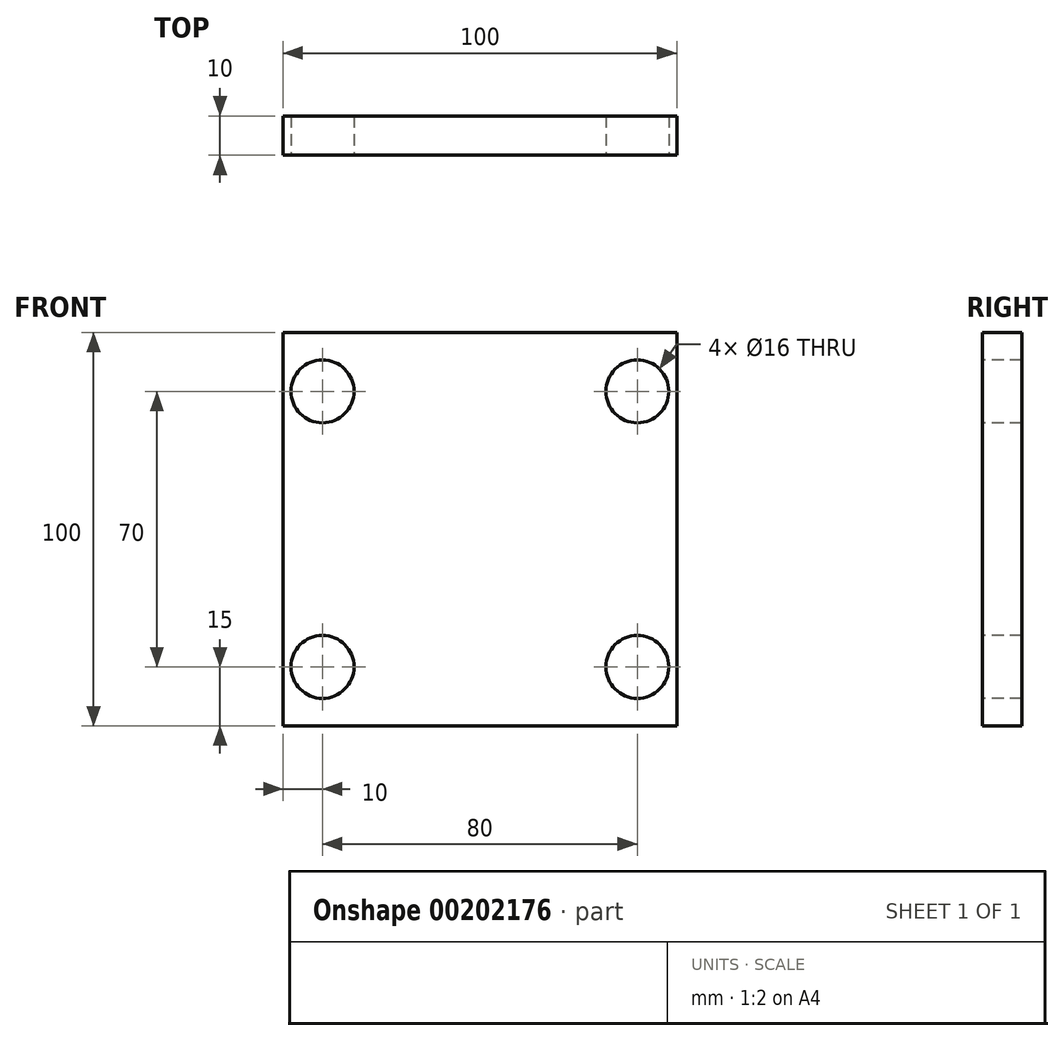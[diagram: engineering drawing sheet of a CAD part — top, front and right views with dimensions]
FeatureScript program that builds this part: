
annotation { "Feature Type Name" : "Feature", "Feature Type Description" : "" }
export const myFeature = defineFeature(function(context is Context, id is Id, definition is map)
    precondition{}
    {
        {
            var Q0;
            Q0=qCreatedBy(makeId("Front.planeOp"),FACE);
            var sketch = newSketch(context, id + "F0", { "sketchPlane" : qUnion([Q0])});
            skLineSegment(sketch, "E0.bottom", {"start": v(50, -50) * mm, "end": v(-50, -50) * mm});
            skLineSegment(sketch, "E0.top", {"start": v(50, 50) * mm, "end": v(-50, 50) * mm});
            skLineSegment(sketch, "E0.left", {"start": v(50, -50) * mm, "end": v(50, 50) * mm});
            skLineSegment(sketch, "E0.right", {"start": v(-50, -50) * mm, "end": v(-50, 50) * mm});
            skPoint(sketch, "E0.middle", {"position": v(0, 0) * mm});
            skSolve(sketch);
        }
        {
            var Q0;
            Q0=makeQuery(id+"F0.imprint","IMPRINT",FACE,{"disambiguationData":[TD([[makeQuery(id+"F0.imprint","IMPRINT",EDGE,{"derivedFrom":sQuery(id+"F0.wireOp",EDGE,"E0.bottom")}),-1.0]])]});
            extrude(context, id + "F1", {"entities" : qUnion([Q0]), "depth" : 10 * mm});
        }
        {
            var Q0;
            Q0=makeQuery(id+"F1.opExtrude","CAP_FACE",FACE,{"disambiguationData":[OSD([sQuery(id+"F0.wireOp",EDGE,"E0.bottom"),sQuery(id+"F0.wireOp",EDGE,"E0.top"),sQuery(id+"F0.wireOp",EDGE,"E0.left"),sQuery(id+"F0.wireOp",EDGE,"E0.right")])],"isStart":false});
            var sketch = newSketch(context, id + "F2", { "sketchPlane" : qUnion([Q0])});
            skLineSegment(sketch, "E1", {"start": v(0, 35) * mm, "end": v(40, 35) * mm, "construction": true});
            skLineSegment(sketch, "E2", {"start": v(0, 35) * mm, "end": v(-40, 35) * mm, "construction": true});
            skLineSegment(sketch, "E3", {"start": v(-40, 35) * mm, "end": v(-40, 0) * mm, "construction": true});
            skPoint(sketch, "E4.start.orphan", {"position": v(0, 50) * mm});
            skLineSegment(sketch, "E5", {"start": v(-40, 0) * mm, "end": v(-40, -35) * mm, "construction": true});
            skLineSegment(sketch, "E6", {"start": v(40, -35) * mm, "end": v(40, 35) * mm, "construction": true});
            skLineSegment(sketch, "E7", {"start": v(-40, -35) * mm, "end": v(40, -35) * mm, "construction": true});
            skSolve(sketch);
        }
        {
            var Q0;
            Q0=sQuery(id+"F2.wireOp",VERTEX,"E3.start");
            var Q1;
            Q1=sQuery(id+"F2.wireOp",VERTEX,"E1.end");
            var Q2;
            Q2=sQuery(id+"F2.wireOp",VERTEX,"E7.start");
            var Q3;
            Q3=sQuery(id+"F2.wireOp",VERTEX,"E7.end");
            var Q4;
            Q4=makeQuery(id+"F1.opExtrude","SWEPT_BODY",BODY,{"disambiguationData":[OSD([sQuery(id+"F0.wireOp",EDGE,"E0.bottom"),sQuery(id+"F0.wireOp",EDGE,"E0.top"),sQuery(id+"F0.wireOp",EDGE,"E0.left"),sQuery(id+"F0.wireOp",EDGE,"E0.right")])]});
            hole(context, id + "F3", {"style" : HoleStyle.SIMPLE, "endStyle" : HoleEndStyle.THROUGH, "holeDiameter" : 16 * mm, "locations" : qUnion([Q0, Q1, Q2, Q3]), "scope" : qUnion([Q4]), "isTappedThrough" : true});
        }
    });
